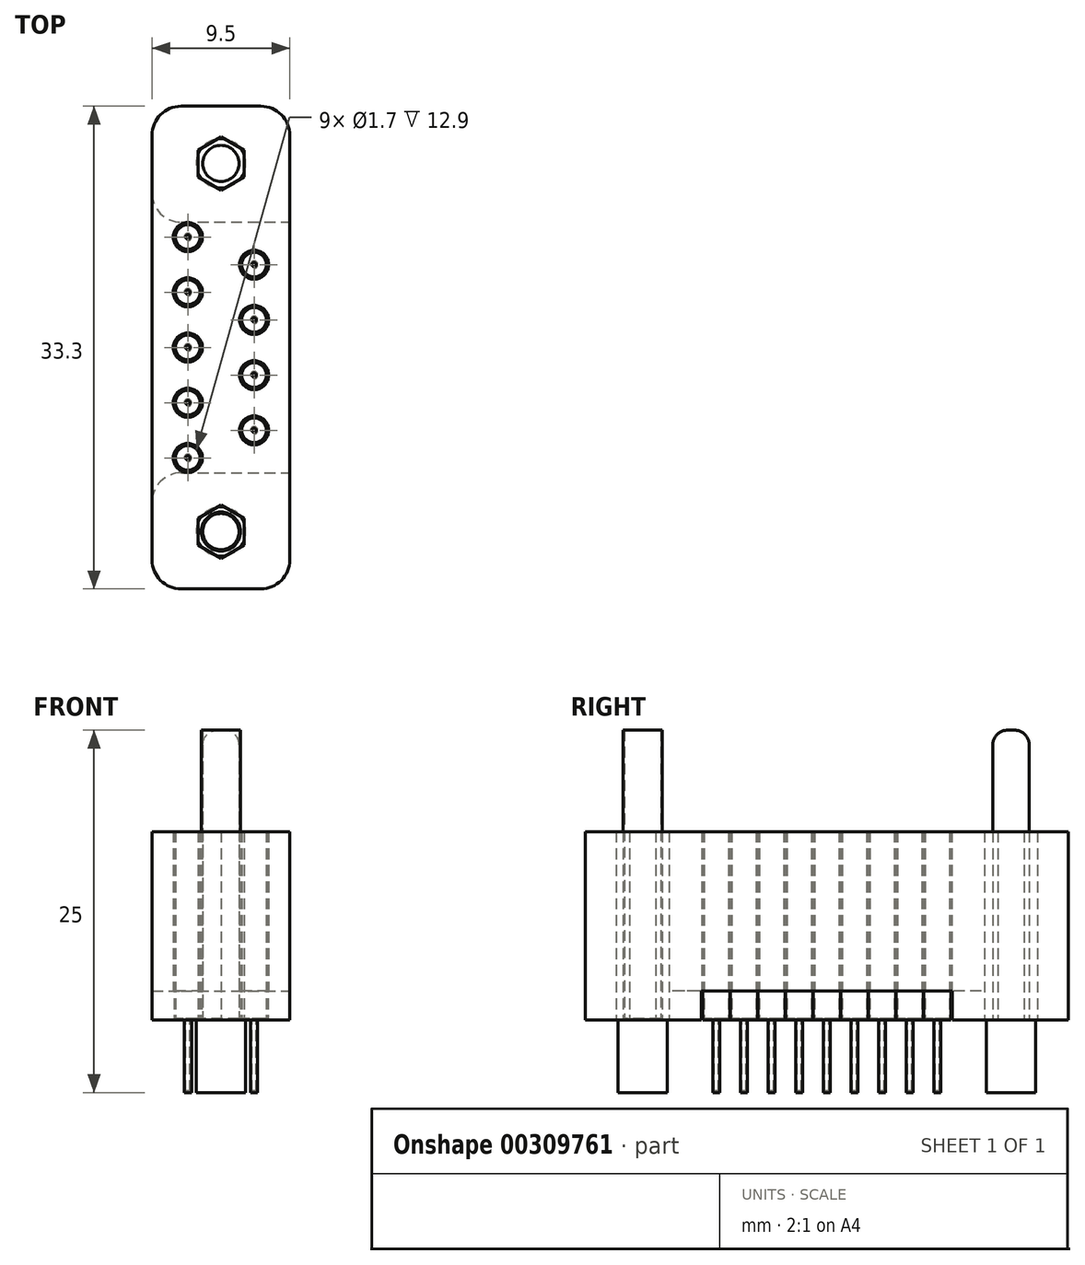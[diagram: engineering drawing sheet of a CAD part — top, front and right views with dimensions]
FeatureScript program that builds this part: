
annotation { "Feature Type Name" : "Feature", "Feature Type Description" : "" }
export const myFeature = defineFeature(function(context is Context, id is Id, definition is map)
    precondition{}
    {
        {
            var Q0;
            Q0=qCreatedBy(makeId("Top.planeOp"),FACE);
            var sketch = newSketch(context, id + "F0", { "sketchPlane" : qUnion([Q0])});
            skLineSegment(sketch, "E0.bottom", {"start": v(4.75, 16.65) * mm, "end": v(-4.75, 16.65) * mm});
            skLineSegment(sketch, "E0.top", {"start": v(4.75, -16.65) * mm, "end": v(-4.75, -16.65) * mm});
            skLineSegment(sketch, "E0.left", {"start": v(4.75, 16.65) * mm, "end": v(4.75, -16.65) * mm});
            skLineSegment(sketch, "E0.right", {"start": v(-4.75, 16.65) * mm, "end": v(-4.75, -16.65) * mm});
            skPoint(sketch, "E0.middle", {"position": v(0, 0) * mm});
            skCircle(sketch, "E1.cCircle", {"center": v(0, 12.7) * mm, "radius": 1.6 * mm, "construction": true});
            skLineSegment(sketch, "E1.0", {"start": v(1.6, 13.62) * mm, "end": v(1.6, 11.78) * mm});
            skLineSegment(sketch, "E1.1", {"start": v(1.6, 11.78) * mm, "end": v(0, 10.86) * mm});
            skLineSegment(sketch, "E1.2", {"start": v(0, 10.86) * mm, "end": v(-1.6, 11.78) * mm});
            skLineSegment(sketch, "E1.3", {"start": v(-1.6, 11.78) * mm, "end": v(-1.6, 13.62) * mm});
            skLineSegment(sketch, "E1.4", {"start": v(-1.6, 13.62) * mm, "end": v(0, 14.54) * mm});
            skLineSegment(sketch, "E1.5", {"start": v(0, 14.54) * mm, "end": v(1.6, 13.62) * mm});
            skPoint(sketch, "E1.0.midPoint", {"position": v(1.6, 12.7) * mm});
            skLineSegment(sketch, "E2.MirrorCS", {"start": v(-1.6, -13.62) * mm, "end": v(0, -14.54) * mm});
            skLineSegment(sketch, "E3.MirrorCS", {"start": v(1.6, -13.62) * mm, "end": v(1.6, -11.78) * mm});
            skLineSegment(sketch, "E4.MirrorCS", {"start": v(0, -10.86) * mm, "end": v(-1.6, -11.78) * mm});
            skCircle(sketch, "E5.MirrorC", {"center": v(0, -12.7) * mm, "radius": 1.6 * mm, "construction": true});
            skPoint(sketch, "E6.MirrorP", {"position": v(1.6, -12.7) * mm});
            skLineSegment(sketch, "E7.MirrorCS", {"start": v(1.6, -11.78) * mm, "end": v(0, -10.86) * mm});
            skLineSegment(sketch, "E8.MirrorCS", {"start": v(0, -14.54) * mm, "end": v(1.6, -13.62) * mm});
            skLineSegment(sketch, "E9.MirrorCS", {"start": v(-1.6, -11.78) * mm, "end": v(-1.6, -13.62) * mm});
            skCircle(sketch, "E10", {"center": v(-2.29, -7.62) * mm, "radius": 1 * mm});
            skCircle(sketch, "E11.1.0.0", {"center": v(-2.29, -3.8) * mm, "radius": 1 * mm});
            skCircle(sketch, "E11.2.0.0", {"center": v(-2.29, 0) * mm, "radius": 1 * mm});
            skLineSegment(sketch, "E11.direction1", {"start": v(-2.29, -7.62) * mm, "end": v(-2.29, -3.8) * mm, "construction": true});
            skCircle(sketch, "E12.0.3.0", {"center": v(-2.29, 3.81) * mm, "radius": 1 * mm});
            skCircle(sketch, "E12.0.4.0", {"center": v(-2.29, 7.62) * mm, "radius": 1 * mm});
            skCircle(sketch, "E13", {"center": v(2.29, -5.71) * mm, "radius": 1 * mm});
            skCircle(sketch, "E14.1.0.0", {"center": v(2.29, -1.9) * mm, "radius": 1 * mm});
            skCircle(sketch, "E14.2.0.0", {"center": v(2.29, 1.9) * mm, "radius": 1 * mm});
            skCircle(sketch, "E14.3.0.0", {"center": v(2.29, 5.71) * mm, "radius": 1 * mm});
            skLineSegment(sketch, "E14.direction1", {"start": v(2.29, -5.71) * mm, "end": v(2.29, -1.9) * mm, "construction": true});
            skSolve(sketch);
        }
        {
            var Q0;
            Q0 = qSketchRegion(id + "F0", true);
            extrude(context, id + "F1", {"entities" : qUnion([Q0]), "depth" : 13 * mm});
        }
        {
            var Q0;
            Q0=makeQuery(id+"F1.opExtrude","SWEPT_FACE",FACE,{"disambiguationData":[OSD([sQuery(id+"F0.wireOp",EDGE,"E0.left")])]});
            var sketch = newSketch(context, id + "F2", { "sketchPlane" : qUnion([Q0])});
            skLineSegment(sketch, "E15.bottom", {"start": v(8.65, 2) * mm, "end": v(-8.65, 2) * mm});
            skLineSegment(sketch, "E15.top", {"start": v(8.65, -2) * mm, "end": v(-8.65, -2) * mm});
            skLineSegment(sketch, "E15.left", {"start": v(8.65, 2) * mm, "end": v(8.65, -2) * mm});
            skLineSegment(sketch, "E15.right", {"start": v(-8.65, 2) * mm, "end": v(-8.65, -2) * mm});
            skPoint(sketch, "E15.middle", {"position": v(0, 0) * mm});
            skSolve(sketch);
        }
        {
            var Q0;
            Q0 = qSketchRegion(id + "F2", true);
            extrude(context, id + "F3", {"entities" : qUnion([Q0]), "operationType" : NewBodyOperationType.REMOVE, "endBound" : BoundingType.THROUGH_ALL, "oppositeDirection" : true, "depth" : 25 * mm});
        }
        {
            var Q0;
            Q0=makeQuery(id+"F1.opExtrude","SWEPT_EDGE",EDGE,{"disambiguationData":[OSD([sQuery(id+"F0.wireOp",EDGE,"E0.top"),sQuery(id+"F0.wireOp",EDGE,"E0.left")])]});
            var Q1;
            Q1=makeQuery(id+"F1.opExtrude","SWEPT_EDGE",EDGE,{"disambiguationData":[OSD([sQuery(id+"F0.wireOp",EDGE,"E0.top"),sQuery(id+"F0.wireOp",EDGE,"E0.right")])]});
            var Q2;
            Q2=makeQuery(id+"F1.opExtrude","SWEPT_EDGE",EDGE,{"disambiguationData":[OSD([sQuery(id+"F0.wireOp",EDGE,"E0.bottom"),sQuery(id+"F0.wireOp",EDGE,"E0.left")])]});
            var Q3;
            Q3=makeQuery(id+"F1.opExtrude","SWEPT_EDGE",EDGE,{"disambiguationData":[OSD([sQuery(id+"F0.wireOp",EDGE,"E0.bottom"),sQuery(id+"F0.wireOp",EDGE,"E0.right")])]});
            var Q4;
            Q4=makeQuery(id+"F3.boolean.opBoolean","INTERSECT",EDGE,{"derivedFrom":[makeQuery(id+"F1.opExtrude","SWEPT_FACE",FACE,{"disambiguationData":[OSD([sQuery(id+"F0.wireOp",EDGE,"E0.right")])]}),makeQuery(id+"F3.opExtrude","SWEPT_FACE",FACE,{"disambiguationData":[OSD([sQuery(id+"F2.wireOp",EDGE,"E15.right")])]})]});
            var Q5;
            Q5=makeQuery(id+"F3.boolean.opBoolean","INTERSECT",EDGE,{"derivedFrom":[makeQuery(id+"F1.opExtrude","SWEPT_FACE",FACE,{"disambiguationData":[OSD([sQuery(id+"F0.wireOp",EDGE,"E0.right")])]}),makeQuery(id+"F3.opExtrude","SWEPT_FACE",FACE,{"disambiguationData":[OSD([sQuery(id+"F2.wireOp",EDGE,"E15.left")])]})]});
            var Q6;
            Q6=makeQuery(id+"F3.boolean.opBoolean","COPY",EDGE,{"derivedFrom":makeQuery(id+"F3.opExtrude","CAP_EDGE",EDGE,{"disambiguationData":[OSD([sQuery(id+"F2.wireOp",EDGE,"E15.left")])],"isStart":true})});
            var Q7;
            Q7=makeQuery(id+"F3.boolean.opBoolean","COPY",EDGE,{"derivedFrom":makeQuery(id+"F3.opExtrude","CAP_EDGE",EDGE,{"disambiguationData":[OSD([sQuery(id+"F2.wireOp",EDGE,"E15.right")])],"isStart":true})});
            fillet(context, id + "F4", {"entities" : qUnion([Q0, Q1, Q2, Q3, Q4, Q5, Q6, Q7]), "radius" : 2 * mm, "tangentPropagation" : true, "allowEdgeOverflow" : false});
        }
        {
            var Q0;
            Q0=makeQuery(id+"F0.imprint","IMPRINT",FACE,{"disambiguationData":[TD([[makeQuery(id+"F0.imprint","IMPRINT",EDGE,{"derivedFrom":sQuery(id+"F0.wireOp",EDGE,"E0.bottom")}),1.0]])]});
            var sketch = newSketch(context, id + "F5", { "sketchPlane" : qUnion([Q0])});
            skCircle(sketch, "E16", {"center": v(-2.29, 7.62) * mm, "radius": 0.25 * mm});
            skCircle(sketch, "E17", {"center": v(-2.29, 3.81) * mm, "radius": 0.25 * mm});
            skCircle(sketch, "E18", {"center": v(2.29, 1.9) * mm, "radius": 0.25 * mm});
            skCircle(sketch, "E19", {"center": v(2.29, 5.71) * mm, "radius": 0.25 * mm});
            skCircle(sketch, "E20", {"center": v(-2.29, 0) * mm, "radius": 0.25 * mm});
            skCircle(sketch, "E21.MirrorC", {"center": v(-2.29, -3.81) * mm, "radius": 0.25 * mm});
            skCircle(sketch, "E22.MirrorC", {"center": v(-2.29, -7.62) * mm, "radius": 0.25 * mm});
            skCircle(sketch, "E23.MirrorC", {"center": v(2.29, -5.71) * mm, "radius": 0.25 * mm});
            skCircle(sketch, "E24.MirrorC", {"center": v(2.29, -1.9) * mm, "radius": 0.25 * mm});
            skSolve(sketch);
        }
        {
            var Q0;
            Q0 = qSketchRegion(id + "F5", true);
            extrude(context, id + "F6", {"entities" : qUnion([Q0]), "oppositeDirection" : true, "depth" : 5 * mm});
        }
        {
            var Q0;
            Q0=makeQuery(id+"F0.imprint","IMPRINT",FACE,{"disambiguationData":[TD([[makeQuery(id+"F0.imprint","IMPRINT",EDGE,{"derivedFrom":sQuery(id+"F0.wireOp",EDGE,"E0.bottom")}),1.0]])]});
            var sketch = newSketch(context, id + "F7", { "sketchPlane" : qUnion([Q0])});
            skCircle(sketch, "E25", {"center": v(-2.29, 7.62) * mm, "radius": 0.95 * mm});
            skCircle(sketch, "E26", {"center": v(-2.29, 3.81) * mm, "radius": 0.95 * mm});
            skCircle(sketch, "E27", {"center": v(2.29, 5.71) * mm, "radius": 0.95 * mm});
            skCircle(sketch, "E28", {"center": v(2.29, 1.9) * mm, "radius": 0.95 * mm});
            skCircle(sketch, "E29", {"center": v(-2.29, 0) * mm, "radius": 0.95 * mm});
            skCircle(sketch, "E30.MirrorC", {"center": v(-2.29, -3.81) * mm, "radius": 0.95 * mm});
            skCircle(sketch, "E31.MirrorC", {"center": v(-2.29, -7.62) * mm, "radius": 0.95 * mm});
            skCircle(sketch, "E32.MirrorC", {"center": v(2.29, -1.9) * mm, "radius": 0.95 * mm});
            skCircle(sketch, "E33.MirrorC", {"center": v(2.29, -5.71) * mm, "radius": 0.95 * mm});
            skSolve(sketch);
        }
        {
            var Q0;
            Q0 = qSketchRegion(id + "F7", true);
            extrude(context, id + "F8", {"entities" : qUnion([Q0]), "operationType" : NewBodyOperationType.ADD, "depth" : 13 * mm});
        }
        {
            var Q0;
            Q0=makeQuery(id+"F8.opExtrude","CAP_FACE",FACE,{"disambiguationData":[OSD([sQuery(id+"F7.wireOp",EDGE,"E25")])],"isStart":false});
            var Q1;
            Q1=makeQuery(id+"F8.opExtrude","CAP_FACE",FACE,{"disambiguationData":[OSD([sQuery(id+"F7.wireOp",EDGE,"E27")])],"isStart":false});
            var Q2;
            Q2=makeQuery(id+"F8.opExtrude","CAP_FACE",FACE,{"disambiguationData":[OSD([sQuery(id+"F7.wireOp",EDGE,"E26")])],"isStart":false});
            var Q3;
            Q3=makeQuery(id+"F8.opExtrude","CAP_FACE",FACE,{"disambiguationData":[OSD([sQuery(id+"F7.wireOp",EDGE,"E28")])],"isStart":false});
            var Q4;
            Q4=makeQuery(id+"F8.opExtrude","CAP_FACE",FACE,{"disambiguationData":[OSD([sQuery(id+"F7.wireOp",EDGE,"E29")])],"isStart":false});
            var Q5;
            Q5=makeQuery(id+"F8.opExtrude","CAP_FACE",FACE,{"disambiguationData":[OSD([sQuery(id+"F7.wireOp",EDGE,"E30.MirrorC")])],"isStart":false});
            var Q6;
            Q6=makeQuery(id+"F8.opExtrude","CAP_FACE",FACE,{"disambiguationData":[OSD([sQuery(id+"F7.wireOp",EDGE,"E32.MirrorC")])],"isStart":false});
            var Q7;
            Q7=makeQuery(id+"F8.opExtrude","CAP_FACE",FACE,{"disambiguationData":[OSD([sQuery(id+"F7.wireOp",EDGE,"E33.MirrorC")])],"isStart":false});
            var Q8;
            Q8=makeQuery(id+"F8.opExtrude","CAP_FACE",FACE,{"disambiguationData":[OSD([sQuery(id+"F7.wireOp",EDGE,"E31.MirrorC")])],"isStart":false});
            shell(context, id + "F9", {"entities" : qUnion([Q0, Q1, Q2, Q3, Q4, Q5, Q6, Q7, Q8]), "thickness" : 0.1 * mm});
        }
        {
            var Q0;
            Q0=makeQuery(id+"F0.imprint","IMPRINT",FACE,{"disambiguationData":[TD([[makeQuery(id+"F0.imprint","IMPRINT",EDGE,{"derivedFrom":sQuery(id+"F0.wireOp",EDGE,"E0.bottom")}),1.0]])]});
            var sketch = newSketch(context, id + "F10", { "sketchPlane" : qUnion([Q0])});
            skCircle(sketch, "E34", {"center": v(0, 12.7) * mm, "radius": 1.25 * mm});
            skCircle(sketch, "E35", {"center": v(0, -12.7) * mm, "radius": 1.35 * mm});
            skSolve(sketch);
        }
        {
            var Q0;
            Q0 = qSketchRegion(id + "F10", true);
            extrude(context, id + "F11", {"entities" : qUnion([Q0]), "depth" : 20 * mm});
        }
        {
            var Q0;
            Q0=makeQuery(id+"F11.opExtrude","CAP_EDGE",EDGE,{"disambiguationData":[OSD([sQuery(id+"F10.wireOp",EDGE,"E34")])],"isStart":false});
            var Q1;
            Q1=makeQuery(id+"F11.opExtrude","CAP_EDGE",EDGE,{"disambiguationData":[OSD([sQuery(id+"F10.wireOp",EDGE,"a7156d45-9b53-4c99-9648-a11054cc19e90.MirrorC")])],"isStart":false});
            fillet(context, id + "F12", {"entities" : qUnion([Q0, Q1]), "radius" : 1 * mm, "tangentPropagation" : true, "allowEdgeOverflow" : false});
        }
        {
            var Q0;
            Q0=makeQuery(id+"F0.imprint","IMPRINT",FACE,{"disambiguationData":[TD([[makeQuery(id+"F0.imprint","IMPRINT",EDGE,{"derivedFrom":sQuery(id+"F0.wireOp",EDGE,"E0.bottom")}),1.0]])]});
            var sketch = newSketch(context, id + "F13", { "sketchPlane" : qUnion([Q0])});
            skCircle(sketch, "E36", {"center": v(0, 12.7) * mm, "radius": 1.7 * mm});
            skCircle(sketch, "E37.MirrorC", {"center": v(0, -12.7) * mm, "radius": 1.7 * mm});
            skSolve(sketch);
        }
        {
            var Q0;
            Q0 = qSketchRegion(id + "F13", true);
            extrude(context, id + "F14", {"entities" : qUnion([Q0]), "oppositeDirection" : true, "depth" : 5 * mm});
        }
        {
            var Q0;
            Q0=makeQuery(id+"F11.opExtrude","CAP_FACE",FACE,{"disambiguationData":[OSD([sQuery(id+"F10.wireOp",EDGE,"E35")])],"isStart":false});
            shell(context, id + "F15", {"entities" : qUnion([Q0]), "thickness" : 0.1 * mm});
        }
    });
